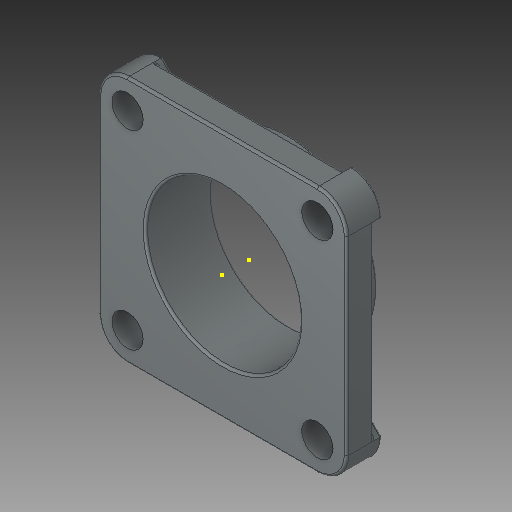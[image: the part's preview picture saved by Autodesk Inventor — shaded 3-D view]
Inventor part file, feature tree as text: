
AUTODESK INVENTOR PART (.ipt)
format: ipt  version: 2019 (Build 230136000, 136)  size: 455,680 bytes
history: native  units: in
note: dims shown in document units (in); Inventor stores cm internally (conversion verified against a paired STEP export)
features: sketch x10, other x3
ambient origin geometry x8: Origin, YZ Plane, XZ Plane, XY Plane, X Axis, Y Axis, Z Axis, Center Point
bodies: Solid1 (feature_tree)
feature tree (13):
  other  "project flange bearing part1_MIR1_MIR1.ipt"
  other  "Solid1::project flange bearing part1_MIR1_MIR1.ipt"
  other  "TaggingFeature1"
  sketch  "Sketch1"  dims[d0=0.3937in]
  sketch  "Sketch2"
  sketch  "Sketch3"
  sketch  "Sketch4"
  sketch  "Sketch5"
  sketch  "Sketch6"
  sketch  "Sketch7"
  sketch  "Sketch8"
  sketch  "Sketch9"
  sketch  "Sketch10"
